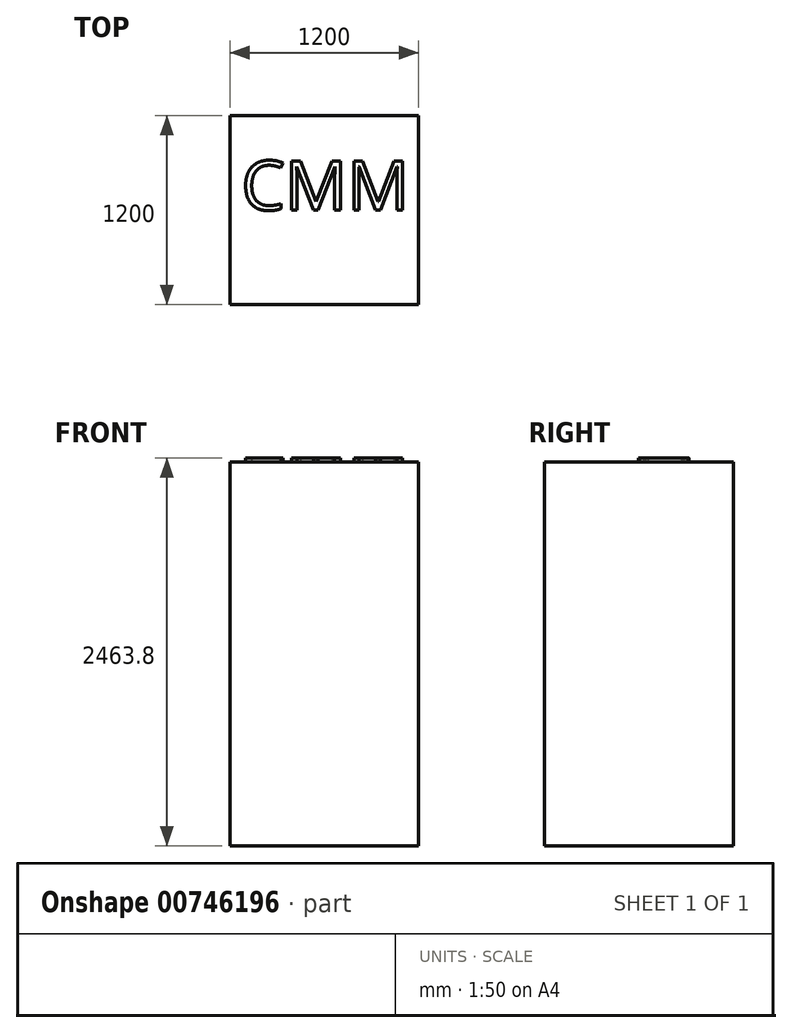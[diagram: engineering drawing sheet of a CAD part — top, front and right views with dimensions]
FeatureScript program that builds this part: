
annotation { "Feature Type Name" : "Feature", "Feature Type Description" : "" }
export const myFeature = defineFeature(function(context is Context, id is Id, definition is map)
    precondition{}
    {
        {
            var Q0;
            Q0=qCreatedBy(makeId("Top.planeOp"),FACE);
            var sketch = newSketch(context, id + "F0", { "sketchPlane" : qUnion([Q0])});
            skLineSegment(sketch, "E0.bottom", {"start": v(600, -600) * mm, "end": v(-600, -600) * mm});
            skLineSegment(sketch, "E0.top", {"start": v(600, 600) * mm, "end": v(-600, 600) * mm});
            skLineSegment(sketch, "E0.left", {"start": v(600, -600) * mm, "end": v(600, 600) * mm});
            skLineSegment(sketch, "E0.right", {"start": v(-600, -600) * mm, "end": v(-600, 600) * mm});
            skPoint(sketch, "E0.middle", {"position": v(0, 0) * mm});
            skSolve(sketch);
        }
        {
            var Q0;
            Q0 = qSketchRegion(id + "F0", true);
            extrude(context, id + "F1", {"entities" : qUnion([Q0]), "depth" : 2438.4 * mm, "offsetDistance" : 25.4 * mm});
        }
        {
            var Q0;
            Q0=makeQuery(id+"F1.opExtrude","CAP_FACE",FACE,{"disambiguationData":[OSD([sQuery(id+"F0.wireOp",EDGE,"E0.bottom"),sQuery(id+"F0.wireOp",EDGE,"E0.top"),sQuery(id+"F0.wireOp",EDGE,"E0.left"),sQuery(id+"F0.wireOp",EDGE,"E0.right")])],"isStart":false});
            var sketch = newSketch(context, id + "F2", { "sketchPlane" : qUnion([Q0])});
            skText(sketch, "E1", { "text": "CMM", "fontName": "OpenSans-Regular.ttf"});
            const initialGuessF2  = {"E1": [-0.52626, 0, 1, 0, 0.31526]};
            skSetInitialGuess(sketch, initialGuessF2);
            skSolve(sketch);
        }
        {
            var Q0;
            Q0 = qSketchRegion(id + "F2", true);
            extrude(context, id + "F3", {"entities" : qUnion([Q0]), "operationType" : NewBodyOperationType.ADD, "depth" : 25.4 * mm, "offsetDistance" : 25.4 * mm});
        }
    });
